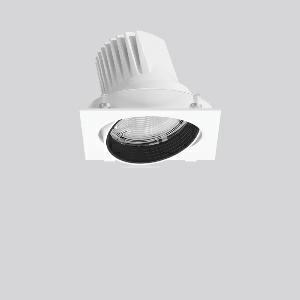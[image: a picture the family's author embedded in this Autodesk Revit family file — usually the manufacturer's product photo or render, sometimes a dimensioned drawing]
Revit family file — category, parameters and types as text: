
# Revit family: magcardo_maxi_722192_002_1_3919
name_source: partatom
category: Lighting Fixtures
units: mm (PartAtom-declared; Revit-internal decimal feet)

## family parameters
Cut with Voids When Loaded = No
Host = Face
Light Source = No
Part Type = Normal
Room Calculation Point = No
Round Connector Dimension = Use Diameter
Shared = No

## types (1)
- MAGCARDO maxi (1 x LED Modul 940, 2950 lm, 4000)
    Apparent Load = 25 VA
    Approval mark = CE
    CIE Flux Codes = 96 100 100 100 100
    Color Rendering = 92
    Color Temperature = 4000
    Default Elevation = 1800 mm
    Description = Series: MAGCARDO maxi
Projector unit for tool-free mounting in separate recessed frame. Luminaire top: die-cast aluminium, powder-coated. Rotation range 356° and swivel range ± 35°. Inner cover prevents view into the false ceiling. Black plastic ring and recessed LED to prevent glare from the side. Optical assembly with lens made of plastic (polycarbonate) for the best homogeneous light distribution - can be changed without tools. Best colour rendering index Ra>90. Magnetic click locking mechanism for quick and convenient installation without tools: insert the recessed frame (1, 2 or 3-lamp) with clamp fastener (no tools required), push the luminaire head with the base plate into the recessed frame and fix magnetically. Including separate LED converter with connecting cable 600 mm.High quality converter without flickering and stroboscopic effect. Through-wiring box (5 pole) available as accessory. The following accessories can be mounted without use of tools: interchangeable lenses, honeycomb louvre, clear and frosted diffusers, white interchangeable plastic ring.Modular design: recessed mounting frame must be ordered separately! 
Colour: traffic white, matt (RAL 9016)
Length: 172 mm
Width: 167 mm
Height: 137 mm
Recess height: 155 mm
Lamp: LED
Socket: without socket
Colour temperature: 4000K
Colour rendering index (CRI): 92
System power: 25 W
Rated luminous flux: 2950 lm
Luminous efficiency: 118 lm/W
Control gear: Regulated power supply
Protection class: II
Type of protection: IP 20
    Height = 0 mm  [stored 0 ft]
    Lamp = 1 x LED Modul 940
    Lamp Light Flux = 2950 lm
    Lamp count = 1
    Length = 172 mm
    Lifetime = 50000 h
    Luminous efficacy = 118 lm/W
    Manufacturer = RZB
    ModVariant = No
    Model = 722192.002.1
    Mounting Place = Ceiling, Wall
    Mounting Type = Recessed
    Number of Poles = 1
    OnlyDefault = Yes
    Power Factor = 1
    Product Name = MAGCARDO maxi
    Product group = Recessed projectors
    ProductGroupID = 401
    Protection Class = Protection class II
    Protection Degree = IP 20
    RLX_Detail_Level = 1
    RLX_Emergency_Light_Flux = 0 lm
    RLX_Emergency_Type = 0
    RLX_Emergency_Type_DB = No
    RlxData = <blob elided: 40133 chars, md5=6219ce39>
    Socket = socket
    Standby Power = 0 W
    System Light Flux = 2950 lm
    System Power = 25 W
    Type Comments = Product without accessories
    Type Image = 722048.002.jpg
    URL = http://relux.com
    VarID = ---
    Voltage = 230 V
    Voltage Range = 220-240 V
    Weight = 0.00 kg
    Width = 167 mm

note: [stored X ft] marks values corroborated as IEEE doubles in the binary element streams (Revit-internal decimal feet)

## geometry (parser evidence)
native form markers: Blend x4, Sweep x10
no freeform markers — native parametric forms only
